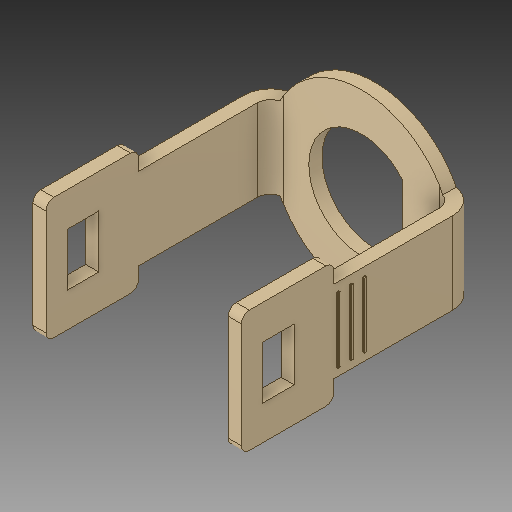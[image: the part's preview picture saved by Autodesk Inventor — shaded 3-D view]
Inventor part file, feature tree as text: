
AUTODESK INVENTOR PART (.ipt)
format: ipt  version: 2019 (Build 230136000, 136)  size: 209,408 bytes
history: mixed  units: mm
features: mirror x1, imported_body x1
ambient origin geometry x8: Origin, YZ Plane, XZ Plane, XY Plane, X Axis, Y Axis, Z Axis, Center Point
bodies: Solid1 (imported_parasolid)
feature tree (2):
  mirror  "Mirror3"
  imported_body  NMx_Import_Brep_tag  [imported B-rep: ~16 faces, bbox_mm=[17.861806, 10.38569, 20.805704]]
